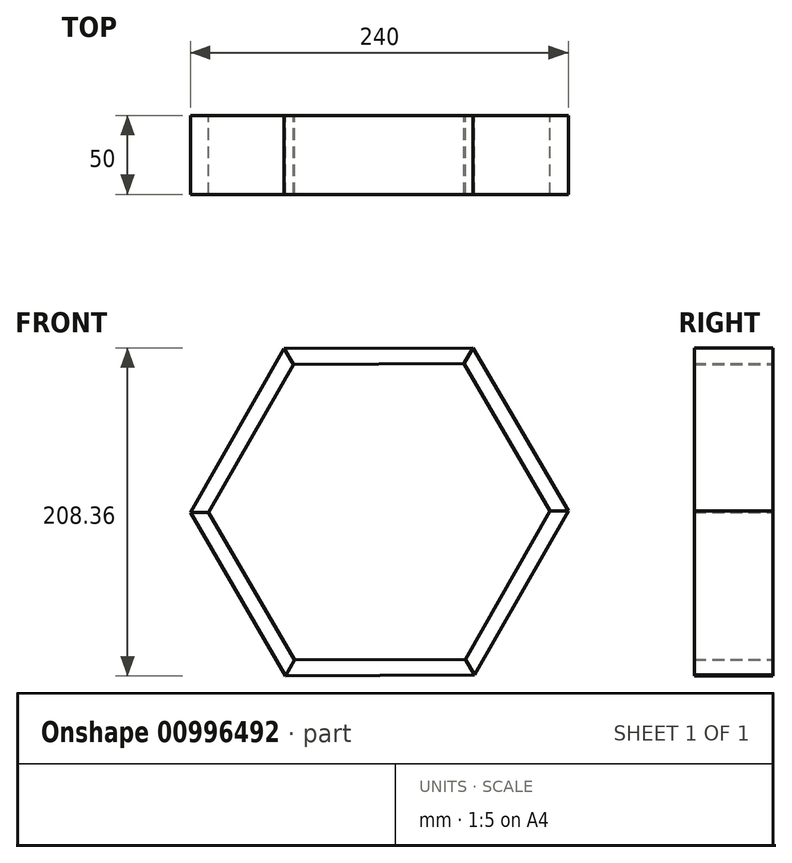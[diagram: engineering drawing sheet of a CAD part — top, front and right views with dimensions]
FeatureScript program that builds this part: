
annotation { "Feature Type Name" : "Feature", "Feature Type Description" : "" }
export const myFeature = defineFeature(function(context is Context, id is Id, definition is map)
    precondition{}
    {
        {
            var Q0;
            Q0=qCreatedBy(makeId("Front.planeOp"),FACE);
            var sketch = newSketch(context, id + "F0", { "sketchPlane" : qUnion([Q0])});
            skCircle(sketch, "E0.cCircle", {"center": v(0, 0) * mm, "radius": 103.92 * mm, "construction": true});
            skLineSegment(sketch, "E0.0", {"start": v(-120, -0.51) * mm, "end": v(-60.45, 103.66) * mm});
            skLineSegment(sketch, "E0.1", {"start": v(-60.45, 103.66) * mm, "end": v(59.55, 104.18) * mm});
            skLineSegment(sketch, "E0.2", {"start": v(59.55, 104.18) * mm, "end": v(120, 0.51) * mm});
            skLineSegment(sketch, "E0.3", {"start": v(120, 0.51) * mm, "end": v(60.45, -103.66) * mm});
            skLineSegment(sketch, "E0.4", {"start": v(60.45, -103.66) * mm, "end": v(-59.55, -104.18) * mm});
            skLineSegment(sketch, "E0.5", {"start": v(-59.55, -104.18) * mm, "end": v(-120, -0.51) * mm});
            skPoint(sketch, "E0.0.midPoint", {"position": v(-90.22, 51.58) * mm});
            skCircle(sketch, "E1.cCircle", {"center": v(0, 0) * mm, "radius": 93.92 * mm, "construction": true});
            skLineSegment(sketch, "E1.0", {"start": v(-108.45, -0.47) * mm, "end": v(-54.63, 93.69) * mm});
            skLineSegment(sketch, "E1.1", {"start": v(-54.63, 93.69) * mm, "end": v(53.82, 94.15) * mm});
            skLineSegment(sketch, "E1.2", {"start": v(53.82, 94.15) * mm, "end": v(108.45, 0.47) * mm});
            skLineSegment(sketch, "E1.3", {"start": v(108.45, 0.47) * mm, "end": v(54.63, -93.69) * mm});
            skLineSegment(sketch, "E1.4", {"start": v(54.63, -93.69) * mm, "end": v(-53.82, -94.15) * mm});
            skLineSegment(sketch, "E1.5", {"start": v(-53.82, -94.15) * mm, "end": v(-108.45, -0.47) * mm});
            skPoint(sketch, "E1.0.midPoint", {"position": v(-81.54, 46.61) * mm});
            skLineSegment(sketch, "E2", {"start": v(-60.45, 103.66) * mm, "end": v(-54.63, 93.69) * mm});
            skLineSegment(sketch, "E3", {"start": v(59.55, 104.18) * mm, "end": v(53.82, 94.15) * mm});
            skLineSegment(sketch, "E4", {"start": v(108.45, 0.47) * mm, "end": v(120, 0.51) * mm});
            skLineSegment(sketch, "E5", {"start": v(54.63, -93.69) * mm, "end": v(60.45, -103.66) * mm});
            skLineSegment(sketch, "E6", {"start": v(-53.82, -94.15) * mm, "end": v(-59.55, -104.18) * mm});
            skLineSegment(sketch, "E7", {"start": v(-120, -0.51) * mm, "end": v(-108.45, -0.47) * mm});
            skSolve(sketch);
        }
        {
            var Q0;
            Q0=makeQuery(id+"F0.imprint","IMPRINT",FACE,{"disambiguationData":[TD([[makeQuery(id+"F0.imprint","IMPRINT",EDGE,{"derivedFrom":sQuery(id+"F0.wireOp",EDGE,"E0.1")}),-1.0]])]});
            extrude(context, id + "F1", {"entities" : qUnion([Q0]), "depth" : 50 * mm, "offsetDistance" : 25 * mm});
        }
        {
            var Q0;
            Q0=makeQuery(id+"F0.imprint","IMPRINT",FACE,{"disambiguationData":[TD([[makeQuery(id+"F0.imprint","IMPRINT",EDGE,{"derivedFrom":sQuery(id+"F0.wireOp",EDGE,"E0.0")}),-1.0]])]});
            extrude(context, id + "F2", {"entities" : qUnion([Q0]), "depth" : 50 * mm, "offsetDistance" : 25 * mm});
        }
        {
            var Q0;
            Q0=makeQuery(id+"F0.imprint","IMPRINT",FACE,{"disambiguationData":[TD([[makeQuery(id+"F0.imprint","IMPRINT",EDGE,{"derivedFrom":sQuery(id+"F0.wireOp",EDGE,"E0.5")}),-1.0]])]});
            extrude(context, id + "F3", {"entities" : qUnion([Q0]), "depth" : 50 * mm, "offsetDistance" : 25 * mm});
        }
        {
            var Q0;
            Q0=makeQuery(id+"F0.imprint","IMPRINT",FACE,{"disambiguationData":[TD([[makeQuery(id+"F0.imprint","IMPRINT",EDGE,{"derivedFrom":sQuery(id+"F0.wireOp",EDGE,"E0.4")}),-1.0]])]});
            extrude(context, id + "F4", {"entities" : qUnion([Q0]), "depth" : 50 * mm, "offsetDistance" : 25 * mm});
        }
        {
            var Q0;
            Q0=makeQuery(id+"F0.imprint","IMPRINT",FACE,{"disambiguationData":[TD([[makeQuery(id+"F0.imprint","IMPRINT",EDGE,{"derivedFrom":sQuery(id+"F0.wireOp",EDGE,"E0.3")}),-1.0]])]});
            extrude(context, id + "F5", {"entities" : qUnion([Q0]), "depth" : 50 * mm, "offsetDistance" : 25 * mm});
        }
        {
            var Q0;
            Q0=makeQuery(id+"F0.imprint","IMPRINT",FACE,{"disambiguationData":[TD([[makeQuery(id+"F0.imprint","IMPRINT",EDGE,{"derivedFrom":sQuery(id+"F0.wireOp",EDGE,"E0.2")}),-1.0]])]});
            extrude(context, id + "F6", {"entities" : qUnion([Q0]), "depth" : 50 * mm, "offsetDistance" : 25 * mm});
        }
    });
